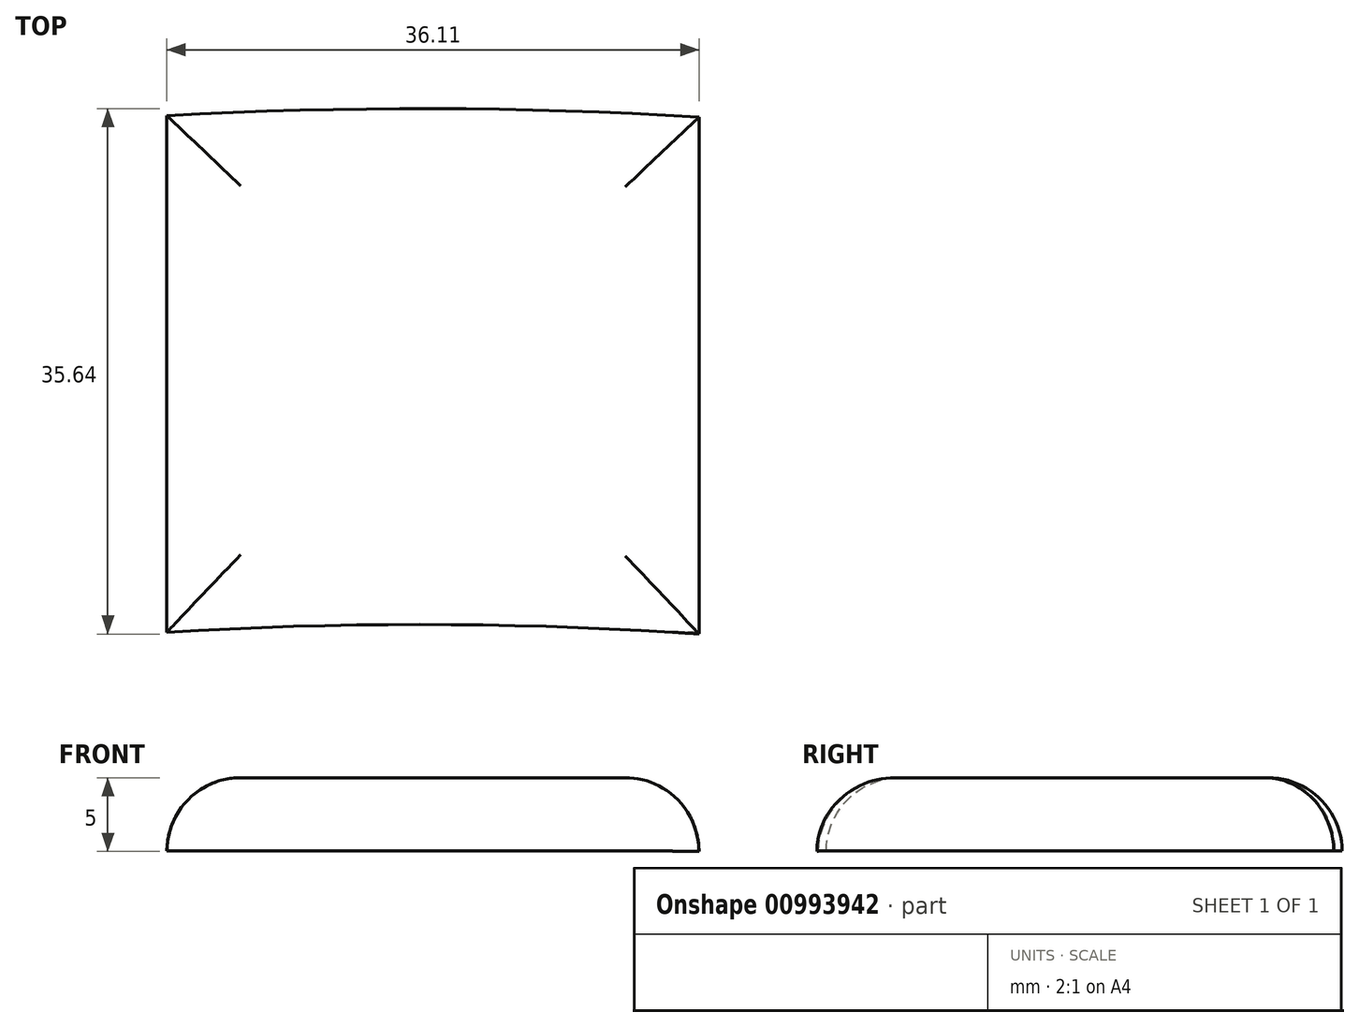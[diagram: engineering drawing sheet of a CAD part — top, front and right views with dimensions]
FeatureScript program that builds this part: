
annotation { "Feature Type Name" : "Feature", "Feature Type Description" : "" }
export const myFeature = defineFeature(function(context is Context, id is Id, definition is map)
    precondition{}
    {
        {
            var Q0;
            Q0=qCreatedBy(makeId("Top.planeOp"),FACE);
            var sketch = newSketch(context, id + "F0", { "sketchPlane" : qUnion([Q0])});
            skCircle(sketch, "E0", {"center": v(0, 0) * mm, "radius": 316.25 * mm});
            skCircle(sketch, "E1", {"center": v(0, 0) * mm, "radius": 281.25 * mm});
            skSolve(sketch);
        }
        {
            var Q0;
            Q0=makeQuery(id+"F0.imprint","IMPRINT",FACE,{"disambiguationData":[TD([[makeQuery(id+"F0.imprint","IMPRINT",EDGE,{"derivedFrom":sQuery(id+"F0.wireOp",EDGE,"E0")}),1.0]])]});
            extrude(context, id + "F1", {"entities" : qUnion([Q0]), "depth" : 10 * mm, "offsetDistance" : 25 * mm});
        }
        {
            var Q0;
            Q0=makeQuery(id+"F1.opExtrude","CAP_FACE",FACE,{"disambiguationData":[OSD([sQuery(id+"F0.wireOp",EDGE,"E0"),sQuery(id+"F0.wireOp",EDGE,"E1")])],"isStart":false});
            var sketch = newSketch(context, id + "F2", { "sketchPlane" : qUnion([Q0])});
            skLineSegment(sketch, "E2.bottom", {"start": v(-17.16, -324.87) * mm, "end": v(18.95, -324.87) * mm});
            skLineSegment(sketch, "E2.top", {"start": v(-17.16, 326.94) * mm, "end": v(18.95, 326.94) * mm});
            skLineSegment(sketch, "E2.left", {"start": v(-17.16, -315.53) * mm, "end": v(-17.16, 326.94) * mm});
            skLineSegment(sketch, "E2.right", {"start": v(18.95, -324.87) * mm, "end": v(18.95, 326.94) * mm});
            skLineSegment(sketch, "E3", {"start": v(-17.16, -315.53) * mm, "end": v(-17.16, -324.87) * mm});
            skSolve(sketch);
        }
        {
            var Q0;
            {var subQ0=sQuery(id+"F2.wireOp",EDGE,"E2.left");var subQ1=makeQuery(id+"F1.opExtrude","CAP_EDGE",EDGE,{"disambiguationData":[OSD([sQuery(id+"F0.wireOp",EDGE,"E0")])],"isStart":false});var subQ2=makeQuery(id+"F2.imprint","INTERSECT",VERTEX,{"derivedFrom":[subQ1,subQ0]});Q0=makeQuery(id+"F2.imprint","IMPRINT",FACE,{"disambiguationData":[TD([[makeQuery(id+"F2.imprint","IMPRINT",EDGE,{"disambiguationData":[TD([[subQ2,1.0]])],"derivedFrom":subQ0}),-1.0]])]});}
            extrude(context, id + "F3", {"entities" : qUnion([Q0]), "operationType" : NewBodyOperationType.ADD, "depth" : 5 * mm, "offsetDistance" : 25 * mm});
        }
        {
            var Q0;
            Q0=makeQuery(id+"F1.opExtrude","CAP_FACE",FACE,{"disambiguationData":[OSD([sQuery(id+"F0.wireOp",EDGE,"E0"),sQuery(id+"F0.wireOp",EDGE,"E1")])],"isStart":false});
            var sketch = newSketch(context, id + "F4", { "sketchPlane" : qUnion([Q0])});
            skLineSegment(sketch, "E4.bottom", {"start": v(417.22, 280.73) * mm, "end": v(-349.96, 280.73) * mm});
            skLineSegment(sketch, "E4.top", {"start": v(417.22, -329.56) * mm, "end": v(-349.96, -329.56) * mm});
            skLineSegment(sketch, "E4.left", {"start": v(417.22, 280.73) * mm, "end": v(417.22, -329.56) * mm});
            skLineSegment(sketch, "E4.right", {"start": v(-349.96, 280.73) * mm, "end": v(-349.96, -329.56) * mm});
            skLineSegment(sketch, "E5.bottom", {"start": v(18.95, 315.68) * mm, "end": v(231.02, 315.68) * mm});
            skLineSegment(sketch, "E5.top", {"start": v(18.95, 280.73) * mm, "end": v(231.02, 280.73) * mm});
            skLineSegment(sketch, "E5.left", {"start": v(18.95, 315.68) * mm, "end": v(18.95, 280.73) * mm});
            skLineSegment(sketch, "E5.right", {"start": v(231.02, 315.68) * mm, "end": v(231.02, 280.73) * mm});
            skLineSegment(sketch, "E6.bottom", {"start": v(-17.16, 315.78) * mm, "end": v(-213.4, 315.78) * mm});
            skLineSegment(sketch, "E6.top", {"start": v(-17.16, 280.73) * mm, "end": v(-213.4, 280.73) * mm});
            skLineSegment(sketch, "E6.left", {"start": v(-17.16, 315.78) * mm, "end": v(-17.16, 280.73) * mm});
            skLineSegment(sketch, "E6.right", {"start": v(-213.4, 315.78) * mm, "end": v(-213.4, 280.73) * mm});
            skSolve(sketch);
        }
        {
            var Q0;
            Q0 = qSketchRegion(id + "F4", true);
            extrude(context, id + "F5", {"entities" : qUnion([Q0]), "operationType" : NewBodyOperationType.REMOVE, "oppositeDirection" : true, "depth" : 84 * mm, "offsetDistance" : 25 * mm});
        }
        {
            var Q0;
            Q0=makeQuery(id+"F5.boolean.opBoolean","MERGE",FACE,{"derivedFrom":[makeQuery(id+"F3.opExtrude","SWEPT_FACE",FACE,{"disambiguationData":[OSD([sQuery(id+"F2.wireOp",EDGE,"E2.right")])]})],"fromTools":[makeQuery(id+"F5.opExtrude","SWEPT_FACE",FACE,{"disambiguationData":[OSD([sQuery(id+"F4.wireOp",EDGE,"E5.left")])]})]});
            var sketch = newSketch(context, id + "F6", { "sketchPlane" : qUnion([Q0])});
            skLineSegment(sketch, "E7.bottom", {"start": v(280.73, 0) * mm, "end": v(317.01, 0) * mm});
            skLineSegment(sketch, "E7.top", {"start": v(280.73, 10.03) * mm, "end": v(317.01, 10.03) * mm});
            skLineSegment(sketch, "E7.left", {"start": v(280.73, 0) * mm, "end": v(280.73, 10.03) * mm});
            skLineSegment(sketch, "E7.right", {"start": v(317.01, 0) * mm, "end": v(317.01, 10.03) * mm});
            skSolve(sketch);
        }
        {
            var Q0;
            {var subQ0=sQuery(id+"F6.wireOp",EDGE,"E7.left");var subQ1=sQuery(id+"F2.wireOp",EDGE,"E2.right");var subQ2=makeQuery(id+"F6.imprint","INTERSECT",VERTEX,{"derivedFrom":[makeQuery(id+"F3.opExtrude","CAP_EDGE",EDGE,{"disambiguationData":[OSD([subQ1])],"isStart":true}),subQ0]});Q0=makeQuery(id+"F6.imprint","IMPRINT",FACE,{"disambiguationData":[TD([[makeQuery(id+"F6.imprint","IMPRINT",EDGE,{"disambiguationData":[TD([[subQ2,-1.0]])],"derivedFrom":subQ0}),-1.0]])]});}
            var Q1;
            {var subQ4=sQuery(id+"F6.wireOp",EDGE,"E7.right");Q1=makeQuery(id+"F6.imprint","IMPRINT",FACE,{"disambiguationData":[TD([[makeQuery(id+"F6.imprint","IMPRINT",EDGE,{"derivedFrom":subQ4}),1.0]])]});}
            extrude(context, id + "F7", {"entities" : qUnion([Q0, Q1]), "operationType" : NewBodyOperationType.REMOVE, "oppositeDirection" : true, "depth" : 42 * mm, "offsetDistance" : 25 * mm});
        }
        {
            var Q0;
            Q0=makeQuery(id+"F3.opExtrude","CAP_EDGE",EDGE,{"disambiguationData":[OSD([sQuery(id+"F0.wireOp",EDGE,"E1")])],"isStart":false});
            var Q1;
            Q1=makeQuery(id+"F3.opExtrude","CAP_EDGE",EDGE,{"disambiguationData":[OSD([sQuery(id+"F2.wireOp",EDGE,"E2.left")])],"isStart":false});
            var Q2;
            Q2=makeQuery(id+"F3.opExtrude","CAP_EDGE",EDGE,{"disambiguationData":[OSD([sQuery(id+"F2.wireOp",EDGE,"E2.right")])],"isStart":false});
            var Q3;
            Q3=makeQuery(id+"F3.opExtrude","CAP_EDGE",EDGE,{"disambiguationData":[OSD([sQuery(id+"F0.wireOp",EDGE,"E0")])],"isStart":false});
            fillet(context, id + "F8", {"entities" : qUnion([Q0, Q1, Q2, Q3]), "radius" : 5 * mm, "tangentPropagation" : true, "allowEdgeOverflow" : false});
        }
    });
